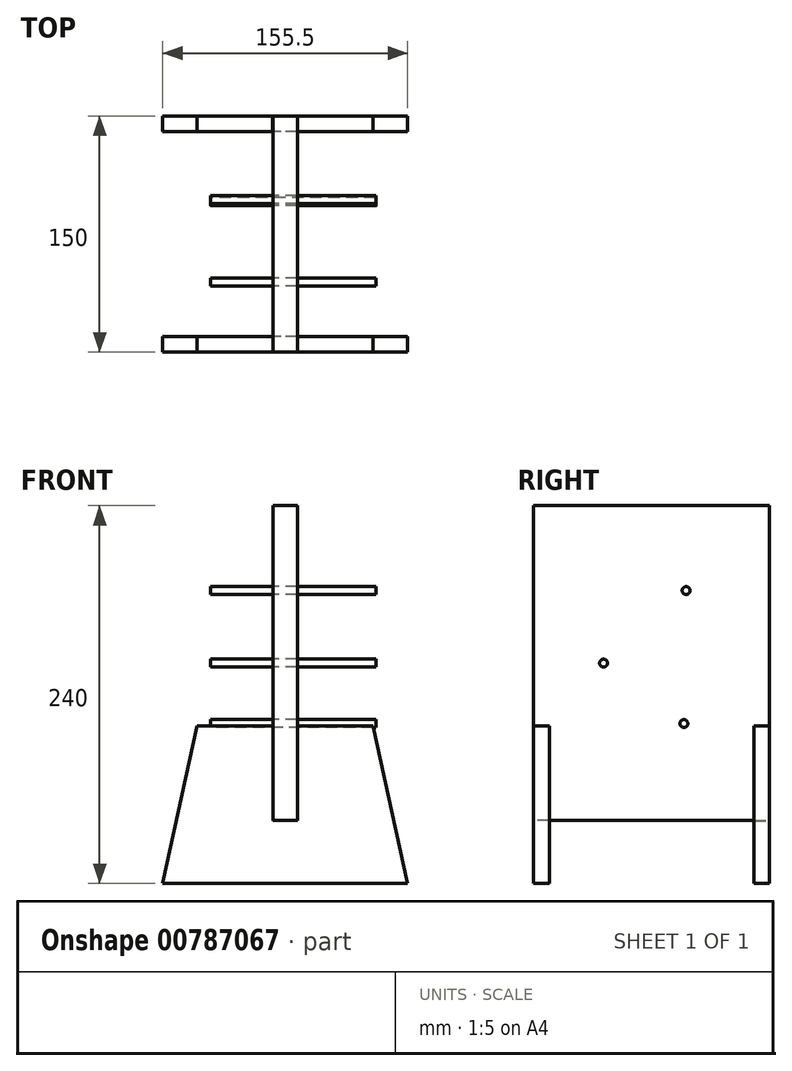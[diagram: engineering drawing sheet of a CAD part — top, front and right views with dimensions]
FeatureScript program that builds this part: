
annotation { "Feature Type Name" : "Feature", "Feature Type Description" : "" }
export const myFeature = defineFeature(function(context is Context, id is Id, definition is map)
    precondition{}
    {
        {
            var Q0;
            Q0=qCreatedBy(makeId("Right.planeOp"),FACE);
            var sketch = newSketch(context, id + "F0", { "sketchPlane" : qUnion([Q0])});
            skLineSegment(sketch, "E0.bottom", {"start": v(-75, 100) * mm, "end": v(75, 100) * mm});
            skLineSegment(sketch, "E0.top", {"start": v(-75, -100) * mm, "end": v(75, -100) * mm});
            skLineSegment(sketch, "E0.left", {"start": v(-75, 100) * mm, "end": v(-75, -100) * mm});
            skLineSegment(sketch, "E0.right", {"start": v(75, 100) * mm, "end": v(75, -100) * mm});
            skPoint(sketch, "E0.middle", {"position": v(0, 0) * mm});
            skSolve(sketch);
        }
        {
            var Q0;
            Q0=makeQuery(id+"F0.imprint","IMPRINT",FACE,{"disambiguationData":[TD([[makeQuery(id+"F0.imprint","IMPRINT",EDGE,{"derivedFrom":sQuery(id+"F0.wireOp",EDGE,"E0.bottom")}),-1.0]])]});
            extrude(context, id + "F1", {"entities" : qUnion([Q0]), "depth" : 15.5 * mm, "offsetDistance" : 25 * mm});
        }
        {
            var Q0;
            Q0=makeQuery(id+"F1.opExtrude","SWEPT_FACE",FACE,{"disambiguationData":[OSD([sQuery(id+"F0.wireOp",EDGE,"E0.left")])]});
            var sketch = newSketch(context, id + "F2", { "sketchPlane" : qUnion([Q0])});
            skLineSegment(sketch, "E1", {"start": v(15.5, -100) * mm, "end": v(15.5, -40) * mm});
            skLineSegment(sketch, "E2", {"start": v(15.5, -40) * mm, "end": v(63.63, -40) * mm});
            skLineSegment(sketch, "E3", {"start": v(63.63, -40) * mm, "end": v(85.5, -140) * mm});
            skLineSegment(sketch, "E4", {"start": v(85.5, -140) * mm, "end": v(15.5, -140) * mm});
            skLineSegment(sketch, "E5", {"start": v(15.5, -140) * mm, "end": v(15.5, -100) * mm});
            skLineSegment(sketch, "E6", {"start": v(7.75, 100) * mm, "end": v(7.75, -100) * mm, "construction": true});
            skLineSegment(sketch, "E7.MirrorCS", {"start": v(0, -40) * mm, "end": v(-48.13, -40) * mm});
            skLineSegment(sketch, "E8.MirrorCS", {"start": v(-48.13, -40) * mm, "end": v(-70, -140) * mm});
            skLineSegment(sketch, "E9.MirrorCS", {"start": v(0, -100) * mm, "end": v(0, -40) * mm});
            skLineSegment(sketch, "E10.MirrorCS", {"start": v(0, -140) * mm, "end": v(0, -100) * mm});
            skLineSegment(sketch, "E11.MirrorCS", {"start": v(-70, -140) * mm, "end": v(0, -140) * mm});
            skLineSegment(sketch, "E12", {"start": v(0, -140) * mm, "end": v(15.5, -140) * mm});
            skLineSegment(sketch, "E13", {"start": v(0, -100) * mm, "end": v(0, -140) * mm});
            skSolve(sketch);
        }
        {
            var Q0;
            {var subQ1=sQuery(id+"F2.wireOp",EDGE,"E1");Q0=makeQuery(id+"F2.imprint","IMPRINT",FACE,{"disambiguationData":[TD([[makeQuery(id+"F2.imprint","IMPRINT",EDGE,{"derivedFrom":subQ1}),1.0]])]});}
            var Q1;
            Q1=makeQuery(id+"F2.imprint","IMPRINT",FACE,{"disambiguationData":[TD([[makeQuery(id+"F2.imprint","IMPRINT",EDGE,{"derivedFrom":sQuery(id+"F2.wireOp",EDGE,"E7.MirrorCS")}),1.0]])]});
            var Q2;
            {var subQ2=sQuery(id+"F2.wireOp",EDGE,"E12");Q2=makeQuery(id+"F2.imprint","IMPRINT",FACE,{"disambiguationData":[TD([[makeQuery(id+"F2.imprint","IMPRINT",EDGE,{"derivedFrom":subQ2}),1.0]])]});}
            extrude(context, id + "F3", {"entities" : qUnion([Q0, Q1, Q2]), "oppositeDirection" : true, "depth" : 10 * mm, "offsetDistance" : 25 * mm});
        }
        {
            var Q0;
            Q0=makeQuery(id+"F3.opExtrude","SWEPT_BODY",BODY,{"disambiguationData":[OSD([sQuery(id+"F0.wireOp",EDGE,"E0.top"),sQuery(id+"F0.wireOp",EDGE,"E0.left"),sQuery(id+"F2.wireOp",EDGE,"E1"),sQuery(id+"F2.wireOp",EDGE,"E2"),sQuery(id+"F2.wireOp",EDGE,"E3"),sQuery(id+"F2.wireOp",EDGE,"E4"),sQuery(id+"F2.wireOp",EDGE,"E5"),sQuery(id+"F2.wireOp",EDGE,"E7.MirrorCS"),sQuery(id+"F2.wireOp",EDGE,"E8.MirrorCS"),sQuery(id+"F2.wireOp",EDGE,"E9.MirrorCS"),sQuery(id+"F2.wireOp",EDGE,"E10.MirrorCS"),sQuery(id+"F2.wireOp",EDGE,"E11.MirrorCS"),sQuery(id+"F2.wireOp",EDGE,"E12")])]});
            transform(context, id + "F4", {"entities" : qUnion([Q0]), "transformType" : TransformType.COPY});
        }
        {
            var Q0;
            Q0=makeQuery(id+"F4.opPattern","COPY",BODY,{"derivedFrom":makeQuery(id+"F3.opExtrude","SWEPT_BODY",BODY,{"disambiguationData":[OSD([sQuery(id+"F0.wireOp",EDGE,"E0.top"),sQuery(id+"F0.wireOp",EDGE,"E0.left"),sQuery(id+"F2.wireOp",EDGE,"E1"),sQuery(id+"F2.wireOp",EDGE,"E2"),sQuery(id+"F2.wireOp",EDGE,"E3"),sQuery(id+"F2.wireOp",EDGE,"E4"),sQuery(id+"F2.wireOp",EDGE,"E5"),sQuery(id+"F2.wireOp",EDGE,"E7.MirrorCS"),sQuery(id+"F2.wireOp",EDGE,"E8.MirrorCS"),sQuery(id+"F2.wireOp",EDGE,"E9.MirrorCS"),sQuery(id+"F2.wireOp",EDGE,"E10.MirrorCS"),sQuery(id+"F2.wireOp",EDGE,"E11.MirrorCS"),sQuery(id+"F2.wireOp",EDGE,"E12")])]}),"instanceName":"1"});
            var Q1;
            Q1=makeQuery(id+"F1.opExtrude","CAP_EDGE",EDGE,{"disambiguationData":[OSD([sQuery(id+"F0.wireOp",EDGE,"E0.top")])],"isStart":false});
            transform(context, id + "F5", {"entities" : qUnion([Q0]), "transformType" : TransformType.TRANSLATION_DISTANCE, "transformDirection" : qUnion([Q1]), "distance" : 140 * mm, "makeCopy" : false});
        }
        {
            var Q0;
            Q0=makeQuery(id+"F1.opExtrude","CAP_FACE",FACE,{"disambiguationData":[OSD([sQuery(id+"F0.wireOp",EDGE,"E0.bottom"),sQuery(id+"F0.wireOp",EDGE,"E0.top"),sQuery(id+"F0.wireOp",EDGE,"E0.left"),sQuery(id+"F0.wireOp",EDGE,"E0.right")])],"isStart":false});
            var sketch = newSketch(context, id + "F6", { "sketchPlane" : qUnion([Q0])});
            skCircle(sketch, "E14", {"center": v(-30.52, 0) * mm, "radius": 2.5 * mm});
            skCircle(sketch, "E15", {"center": v(20.54, -38.43) * mm, "radius": 2.5 * mm});
            skCircle(sketch, "E16", {"center": v(21.94, 46.06) * mm, "radius": 2.5 * mm});
            skSolve(sketch);
        }
        {
            var Q0;
            Q0=makeQuery(id+"F6.imprint","IMPRINT",FACE,{"disambiguationData":[TD([[makeQuery(id+"F6.imprint","IMPRINT",EDGE,{"derivedFrom":sQuery(id+"F6.wireOp",EDGE,"E16")}),1.0]])]});
            var Q1;
            Q1=makeQuery(id+"F6.imprint","IMPRINT",FACE,{"disambiguationData":[TD([[makeQuery(id+"F6.imprint","IMPRINT",EDGE,{"derivedFrom":sQuery(id+"F6.wireOp",EDGE,"E14")}),1.0]])]});
            var Q2;
            Q2=makeQuery(id+"F6.imprint","IMPRINT",FACE,{"disambiguationData":[TD([[makeQuery(id+"F6.imprint","IMPRINT",EDGE,{"derivedFrom":sQuery(id+"F6.wireOp",EDGE,"E15")}),1.0]])]});
            extrude(context, id + "F7", {"entities" : qUnion([Q0, Q1, Q2]), "depth" : 50 * mm, "offsetDistance" : 25 * mm, "hasSecondDirection" : true, "secondDirectionOppositeDirection" : true, "secondDirectionDepth" : 55 * mm});
        }
        {
            var Q0;
            Q0=makeQuery(id+"F4.opPattern","COPY",FACE,{"derivedFrom":makeQuery(id+"F3.opExtrude","CAP_FACE",FACE,{"disambiguationData":[OSD([sQuery(id+"F0.wireOp",EDGE,"E0.top"),sQuery(id+"F0.wireOp",EDGE,"E0.left"),sQuery(id+"F2.wireOp",EDGE,"E1"),sQuery(id+"F2.wireOp",EDGE,"E2"),sQuery(id+"F2.wireOp",EDGE,"E3"),sQuery(id+"F2.wireOp",EDGE,"E4"),sQuery(id+"F2.wireOp",EDGE,"E5"),sQuery(id+"F2.wireOp",EDGE,"E7.MirrorCS"),sQuery(id+"F2.wireOp",EDGE,"E8.MirrorCS"),sQuery(id+"F2.wireOp",EDGE,"E9.MirrorCS"),sQuery(id+"F2.wireOp",EDGE,"E10.MirrorCS"),sQuery(id+"F2.wireOp",EDGE,"E11.MirrorCS"),sQuery(id+"F2.wireOp",EDGE,"E12")])],"isStart":false}),"instanceName":"1"});
            var sketch = newSketch(context, id + "F8", { "sketchPlane" : qUnion([Q0])});
            skLineSegment(sketch, "E17", {"start": v(-15.65, -40) * mm, "end": v(-15.65, -100.1) * mm});
            skLineSegment(sketch, "E18", {"start": v(-15.65, -100.1) * mm, "end": v(0.15, -100.1) * mm});
            skLineSegment(sketch, "E19", {"start": v(0.15, -100.1) * mm, "end": v(0.15, -40) * mm});
            skSolve(sketch);
        }
        {
            var Q0;
            {var subQ3=sQuery(id+"F8.wireOp",EDGE,"E17");Q0=makeQuery(id+"F8.imprint","IMPRINT",FACE,{"disambiguationData":[TD([[makeQuery(id+"F8.imprint","IMPRINT",EDGE,{"derivedFrom":subQ3}),1.0]])]});}
            extrude(context, id + "F9", {"entities" : qUnion([Q0]), "operationType" : NewBodyOperationType.REMOVE, "endBound" : BoundingType.UP_TO_NEXT, "oppositeDirection" : true, "depth" : 25 * mm, "offsetDistance" : 25 * mm});
        }
        {
            var Q0;
            Q0=makeQuery(id+"F4.opPattern","COPY",BODY,{"derivedFrom":makeQuery(id+"F3.opExtrude","SWEPT_BODY",BODY,{"disambiguationData":[OSD([sQuery(id+"F0.wireOp",EDGE,"E0.top"),sQuery(id+"F0.wireOp",EDGE,"E0.left"),sQuery(id+"F2.wireOp",EDGE,"E1"),sQuery(id+"F2.wireOp",EDGE,"E2"),sQuery(id+"F2.wireOp",EDGE,"E3"),sQuery(id+"F2.wireOp",EDGE,"E4"),sQuery(id+"F2.wireOp",EDGE,"E7.MirrorCS"),sQuery(id+"F2.wireOp",EDGE,"E8.MirrorCS"),sQuery(id+"F2.wireOp",EDGE,"E9.MirrorCS"),sQuery(id+"F2.wireOp",EDGE,"E11.MirrorCS"),sQuery(id+"F2.wireOp",EDGE,"E12")])]}),"instanceName":"1"});
            transform(context, id + "F10", {"entities" : qUnion([Q0]), "transformType" : TransformType.TRANSLATION_3D, "dx" : 0 * mm, "dy" : 0 * mm, "dz" : 0 * mm, "makeCopy" : true});
        }
    });
